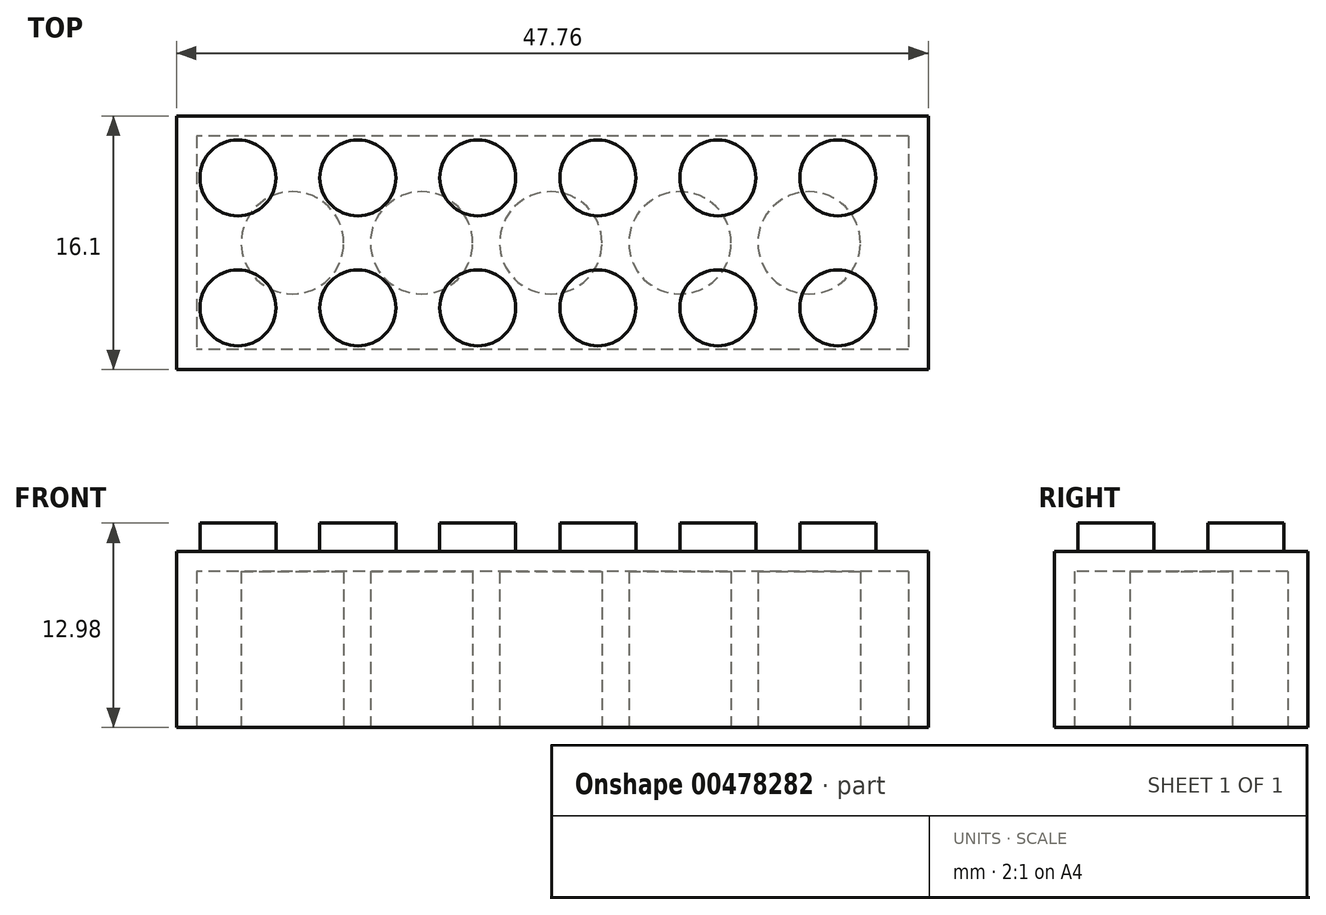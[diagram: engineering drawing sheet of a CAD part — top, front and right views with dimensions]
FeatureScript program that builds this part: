
annotation { "Feature Type Name" : "Feature", "Feature Type Description" : "" }
export const myFeature = defineFeature(function(context is Context, id is Id, definition is map)
    precondition{}
    {
        {
            var Q0;
            Q0=qCreatedBy(makeId("Top.planeOp"),FACE);
            var sketch = newSketch(context, id + "F0", { "sketchPlane" : qUnion([Q0])});
            skLineSegment(sketch, "E0.bottom", {"start": v(23.88, -8.05) * mm, "end": v(-23.88, -8.05) * mm});
            skLineSegment(sketch, "E0.top", {"start": v(23.88, 8.05) * mm, "end": v(-23.88, 8.05) * mm});
            skLineSegment(sketch, "E0.left", {"start": v(23.88, -8.05) * mm, "end": v(23.88, 8.05) * mm});
            skLineSegment(sketch, "E0.right", {"start": v(-23.88, -8.05) * mm, "end": v(-23.88, 8.05) * mm});
            skPoint(sketch, "E0.middle", {"position": v(0, 0) * mm});
            skSolve(sketch);
        }
        {
            var Q0;
            Q0 = qSketchRegion(id + "F0", true);
            extrude(context, id + "F1", {"entities" : qUnion([Q0]), "endBound" : BoundingType.SYMMETRIC, "depth" : 11.18 * mm});
        }
        {
            var Q0;
            Q0=makeQuery(id+"F1.opExtrude","CAP_FACE",FACE,{"disambiguationData":[OSD([sQuery(id+"F0.wireOp",EDGE,"E0.bottom"),sQuery(id+"F0.wireOp",EDGE,"E0.top"),sQuery(id+"F0.wireOp",EDGE,"E0.left"),sQuery(id+"F0.wireOp",EDGE,"E0.right")])],"isStart":false});
            var sketch = newSketch(context, id + "F2", { "sketchPlane" : qUnion([Q0])});
            skCircle(sketch, "E1", {"center": v(-19.98, 4.13) * mm, "radius": 2.41 * mm});
            skCircle(sketch, "E2.1.0.0", {"center": v(-12.36, 4.13) * mm, "radius": 2.41 * mm});
            skCircle(sketch, "E2.2.0.0", {"center": v(-4.74, 4.13) * mm, "radius": 2.41 * mm});
            skCircle(sketch, "E2.3.0.0", {"center": v(2.88, 4.13) * mm, "radius": 2.41 * mm});
            skCircle(sketch, "E2.4.0.0", {"center": v(10.5, 4.13) * mm, "radius": 2.41 * mm});
            skLineSegment(sketch, "E2.direction1", {"start": v(-19.98, 4.13) * mm, "end": v(-12.36, 4.13) * mm, "construction": true});
            skCircle(sketch, "E3.MirrorC", {"center": v(-19.98, -4.13) * mm, "radius": 2.41 * mm});
            skCircle(sketch, "E4.MirrorC", {"center": v(-12.36, -4.13) * mm, "radius": 2.41 * mm});
            skCircle(sketch, "E5.MirrorC", {"center": v(-4.74, -4.13) * mm, "radius": 2.41 * mm});
            skCircle(sketch, "E6.MirrorC", {"center": v(2.88, -4.13) * mm, "radius": 2.41 * mm});
            skCircle(sketch, "E7.MirrorC", {"center": v(10.5, -4.13) * mm, "radius": 2.41 * mm});
            skCircle(sketch, "E8.0.5.0", {"center": v(18.12, 4.13) * mm, "radius": 2.41 * mm});
            skCircle(sketch, "E9.MirrorC", {"center": v(18.12, -4.13) * mm, "radius": 2.41 * mm});
            skSolve(sketch);
        }
        {
            var Q0;
            Q0 = qSketchRegion(id + "F2", true);
            var Q1;
            Q1=makeQuery(id+"F2.imprint","IMPRINT",FACE,{"disambiguationData":[TD([[makeQuery(id+"F2.imprint","IMPRINT",EDGE,{"derivedFrom":sQuery(id+"F2.wireOp",EDGE,"E8.0.5.0")}),1.0]])]});
            extrude(context, id + "F3", {"entities" : qUnion([Q0, Q1]), "operationType" : NewBodyOperationType.ADD, "depth" : 1.8 * mm});
        }
        {
            var Q0;
            Q0=makeQuery(id+"F1.opExtrude","CAP_FACE",FACE,{"disambiguationData":[OSD([sQuery(id+"F0.wireOp",EDGE,"E0.bottom"),sQuery(id+"F0.wireOp",EDGE,"E0.top"),sQuery(id+"F0.wireOp",EDGE,"E0.left"),sQuery(id+"F0.wireOp",EDGE,"E0.right")])],"isStart":true});
            var sketch = newSketch(context, id + "F4", { "sketchPlane" : qUnion([Q0])});
            skCircle(sketch, "E10", {"center": v(-16.51, 0) * mm, "radius": 3.25 * mm});
            skCircle(sketch, "E11.1.0.0", {"center": v(-8.3, 0) * mm, "radius": 3.25 * mm});
            skCircle(sketch, "E11.2.0.0", {"center": v(-0.1, 0) * mm, "radius": 3.25 * mm});
            skCircle(sketch, "E11.3.0.0", {"center": v(8.1, 0) * mm, "radius": 3.25 * mm});
            skCircle(sketch, "E11.4.0.0", {"center": v(16.3, 0) * mm, "radius": 3.25 * mm});
            skLineSegment(sketch, "E11.direction1", {"start": v(-16.51, 0) * mm, "end": v(-8.3, 0) * mm, "construction": true});
            skSolve(sketch);
        }
        {
            var Q0;
            Q0=makeQuery(id+"F4.imprint","IMPRINT",FACE,{"disambiguationData":[TD([[makeQuery(id+"F4.imprint","IMPRINT",EDGE,{"derivedFrom":sQuery(id+"F4.wireOp",EDGE,"E10")}),-1.0]])]});
            var sketch = newSketch(context, id + "F5", { "sketchPlane" : qUnion([Q0])});
            skLineSegment(sketch, "E12.bottom", {"start": v(22.6, -6.78) * mm, "end": v(-22.6, -6.78) * mm});
            skLineSegment(sketch, "E12.top", {"start": v(22.6, 6.78) * mm, "end": v(-22.6, 6.78) * mm});
            skLineSegment(sketch, "E12.left", {"start": v(22.6, -6.78) * mm, "end": v(22.6, 6.78) * mm});
            skLineSegment(sketch, "E12.right", {"start": v(-22.6, -6.78) * mm, "end": v(-22.6, 6.78) * mm});
            skPoint(sketch, "E12.middle", {"position": v(0, 0) * mm});
            skPoint(sketch, "E13.middle", {"position": v(22.6, 12.43) * mm});
            skSolve(sketch);
        }
        {
            var Q0;
            Q0=makeQuery(id+"F5.imprint","IMPRINT",FACE,{"disambiguationData":[TD([[makeQuery(id+"F5.imprint","IMPRINT",EDGE,{"derivedFrom":sQuery(id+"F5.wireOp",EDGE,"E12.bottom")}),-1.0]])]});
            extrude(context, id + "F6", {"entities" : qUnion([Q0]), "operationType" : NewBodyOperationType.REMOVE, "oppositeDirection" : true, "depth" : 9.9 * mm});
        }
    });
